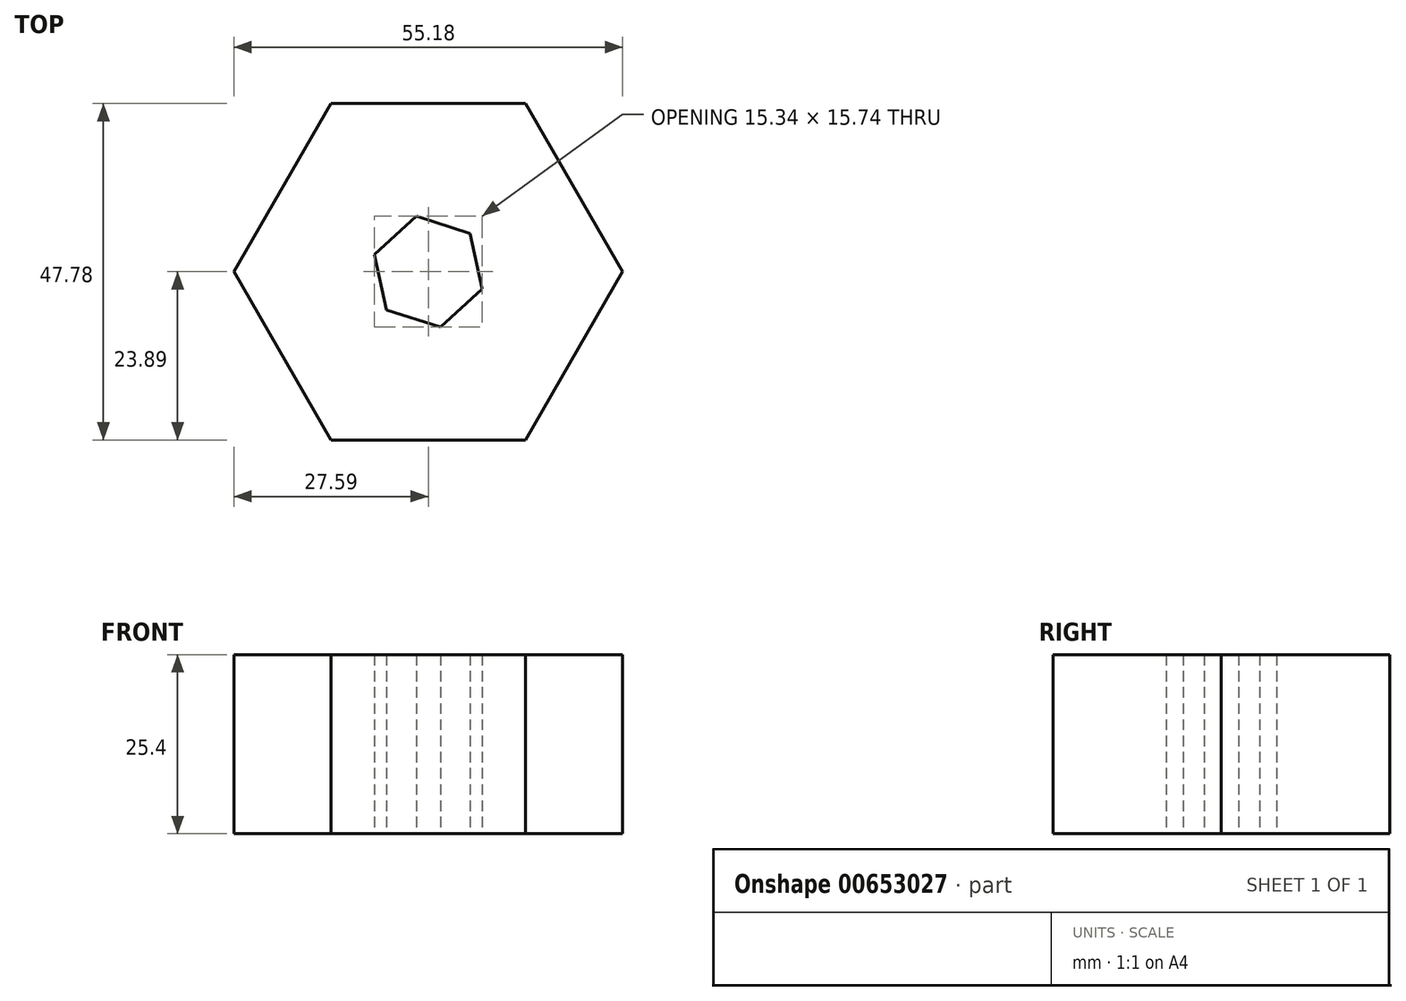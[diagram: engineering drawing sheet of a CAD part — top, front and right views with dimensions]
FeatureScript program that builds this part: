
annotation { "Feature Type Name" : "Feature", "Feature Type Description" : "" }
export const myFeature = defineFeature(function(context is Context, id is Id, definition is map)
    precondition{}
    {
        {
            var Q0;
            Q0=qCreatedBy(makeId("Top.planeOp"),FACE);
            var sketch = newSketch(context, id + "F0", { "sketchPlane" : qUnion([Q0])});
            skCircle(sketch, "E0.cCircle", {"center": v(0, 0) * mm, "radius": 23.89 * mm, "construction": true});
            skLineSegment(sketch, "E0.0", {"start": v(-13.8, 23.89) * mm, "end": v(13.8, 23.89) * mm});
            skLineSegment(sketch, "E0.1", {"start": v(13.8, 23.89) * mm, "end": v(27.59, 0) * mm});
            skLineSegment(sketch, "E0.2", {"start": v(27.59, 0) * mm, "end": v(13.8, -23.89) * mm});
            skLineSegment(sketch, "E0.3", {"start": v(13.8, -23.89) * mm, "end": v(-13.8, -23.89) * mm});
            skLineSegment(sketch, "E0.4", {"start": v(-13.8, -23.89) * mm, "end": v(-27.59, 0) * mm});
            skLineSegment(sketch, "E0.5", {"start": v(-27.59, 0) * mm, "end": v(-13.8, 23.89) * mm});
            skPoint(sketch, "E0.0.midPoint", {"position": v(0, 23.89) * mm});
            skCircle(sketch, "E1.cCircle", {"center": v(0, 0) * mm, "radius": 6.97 * mm, "construction": true});
            skLineSegment(sketch, "E1.0", {"start": v(-1.72, 7.87) * mm, "end": v(5.96, 5.42) * mm});
            skLineSegment(sketch, "E1.1", {"start": v(5.96, 5.42) * mm, "end": v(7.67, -2.45) * mm});
            skLineSegment(sketch, "E1.2", {"start": v(7.67, -2.45) * mm, "end": v(1.72, -7.87) * mm});
            skLineSegment(sketch, "E1.3", {"start": v(1.72, -7.87) * mm, "end": v(-5.96, -5.42) * mm});
            skLineSegment(sketch, "E1.4", {"start": v(-5.96, -5.42) * mm, "end": v(-7.67, 2.45) * mm});
            skLineSegment(sketch, "E1.5", {"start": v(-7.67, 2.45) * mm, "end": v(-1.72, 7.87) * mm});
            skPoint(sketch, "E1.0.midPoint", {"position": v(2.12, 6.64) * mm});
            skSolve(sketch);
        }
        {
            var Q0;
            Q0 = qSketchRegion(id + "F0", true);
            extrude(context, id + "F1", {"entities" : qUnion([Q0]), "depth" : 25.4 * mm, "offsetDistance" : 25.4 * mm});
        }
    });
